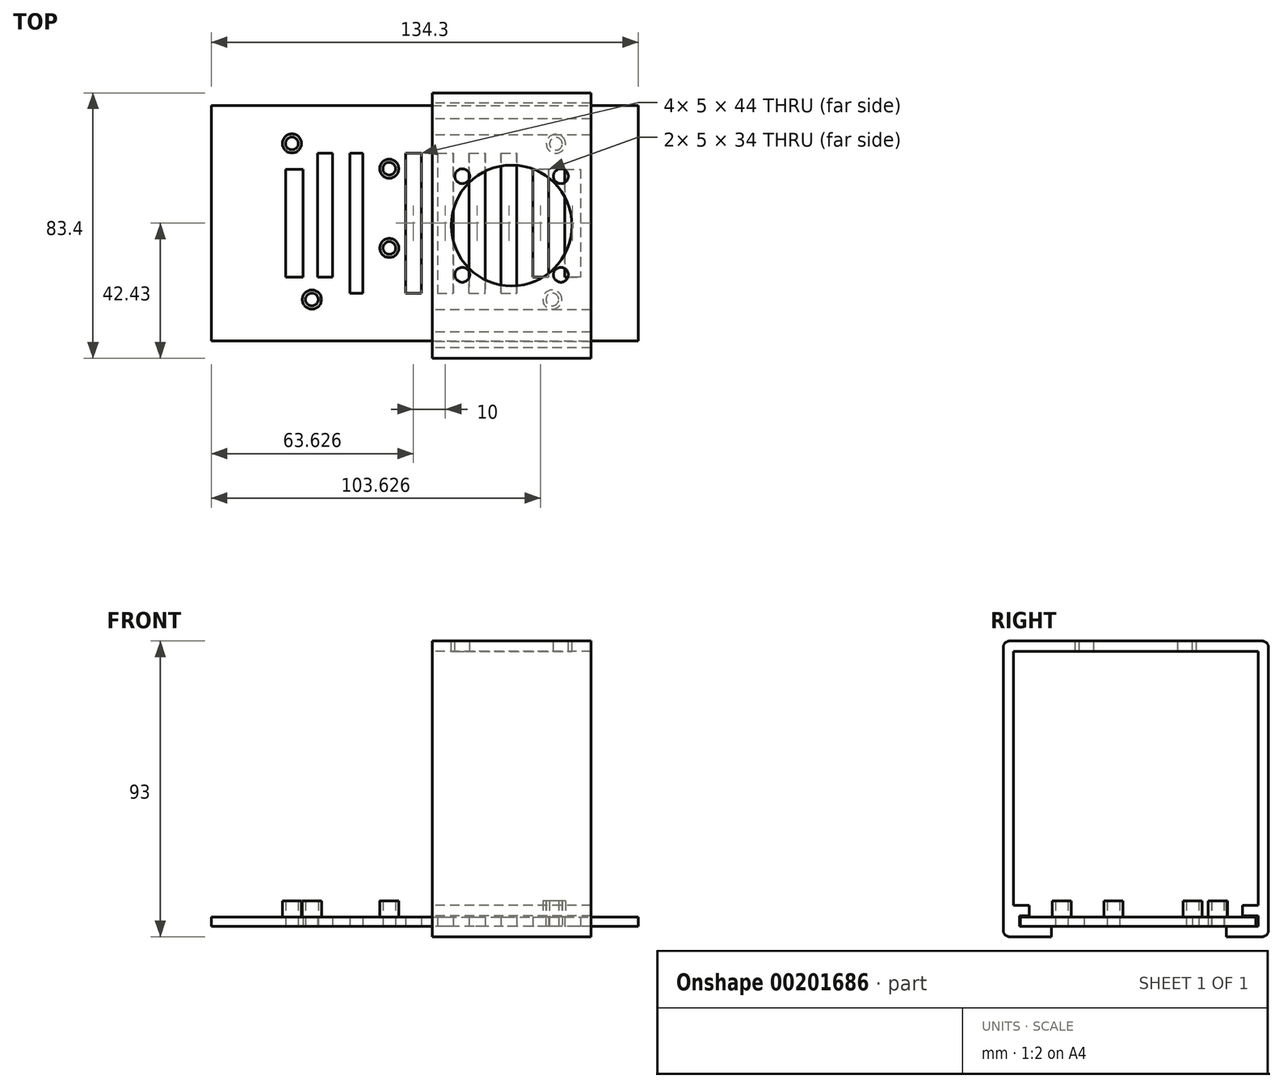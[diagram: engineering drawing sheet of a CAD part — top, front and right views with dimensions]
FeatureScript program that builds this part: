
annotation { "Feature Type Name" : "Feature", "Feature Type Description" : "" }
export const myFeature = defineFeature(function(context is Context, id is Id, definition is map)
    precondition{}
    {
        {
            var Q0;
            Q0=qCreatedBy(makeId("Top.planeOp"),FACE);
            var sketch = newSketch(context, id + "F0", { "sketchPlane" : qUnion([Q0])});
            skLineSegment(sketch, "E0.bottom", {"start": v(-46.5, 27) * mm, "end": v(48, 27) * mm});
            skLineSegment(sketch, "E0.top", {"start": v(-46.75, -27) * mm, "end": v(48, -27) * mm});
            skLineSegment(sketch, "E0.left", {"start": v(-49.5, 22.5) * mm, "end": v(-49.5, -14.5) * mm});
            skLineSegment(sketch, "E0.right", {"start": v(48, 27) * mm, "end": v(48, 23.31) * mm});
            skCircle(sketch, "E1", {"center": v(-44.1, 25.1) * mm, "radius": 2 * mm});
            skCircle(sketch, "E2", {"center": v(-37.82, -24) * mm, "radius": 2 * mm});
            skCircle(sketch, "E3", {"center": v(-13.47, -7.8) * mm, "radius": 2 * mm});
            skCircle(sketch, "E4", {"center": v(38.9, 24.99) * mm, "radius": 2 * mm});
            skCircle(sketch, "E5", {"center": v(37.78, -24) * mm, "radius": 2 * mm});
            skLineSegment(sketch, "E6.bottom", {"start": v(-49.5, -14.5) * mm, "end": v(-46.75, -14.5) * mm});
            skLineSegment(sketch, "E6.right", {"start": v(-46.75, -14.5) * mm, "end": v(-46.75, -27) * mm});
            skCircle(sketch, "E7", {"center": v(-13.52, 17.15) * mm, "radius": 2 * mm});
            skLineSegment(sketch, "E8.bottom", {"start": v(48, -17.5) * mm, "end": v(54.8, -17.5) * mm});
            skLineSegment(sketch, "E8.top", {"start": v(48, -5.37) * mm, "end": v(54.8, -5.37) * mm});
            skLineSegment(sketch, "E8.right", {"start": v(54.8, -17.5) * mm, "end": v(54.8, -5.37) * mm});
            skLineSegment(sketch, "E9.bottom", {"start": v(48, 23.31) * mm, "end": v(49.6, 23.31) * mm});
            skLineSegment(sketch, "E9.top", {"start": v(48, 14.31) * mm, "end": v(49.6, 14.31) * mm});
            skLineSegment(sketch, "E9.right", {"start": v(49.6, 23.31) * mm, "end": v(49.6, 14.31) * mm});
            skLineSegment(sketch, "E10.trimOffspring", {"start": v(48, 14.31) * mm, "end": v(48, -5.37) * mm});
            skLineSegment(sketch, "E11.trimOffspring", {"start": v(48, -17.5) * mm, "end": v(48, -27) * mm});
            skLineSegment(sketch, "E12", {"start": v(-49.5, 22.5) * mm, "end": v(-46.5, 27) * mm});
            skLineSegment(sketch, "E13.bottom", {"start": v(-69.5, -37) * mm, "end": v(64.8, -37) * mm});
            skLineSegment(sketch, "E13.left", {"start": v(-69.5, -37) * mm, "end": v(-69.5, 37) * mm});
            skLineSegment(sketch, "E13.right", {"start": v(64.8, -37) * mm, "end": v(64.8, 37) * mm});
            skLineSegment(sketch, "E14", {"start": v(-69.5, 37) * mm, "end": v(64.8, 37) * mm});
            skSolve(sketch);
        }
        {
            var Q0;
            Q0=makeQuery(id+"F0.imprint","IMPRINT",FACE,{"disambiguationData":[TD([[makeQuery(id+"F0.imprint","IMPRINT",EDGE,{"derivedFrom":sQuery(id+"F0.wireOp",EDGE,"E0.top")}),-1.0]])]});
            var Q1;
            Q1=makeQuery(id+"F0.imprint","IMPRINT",FACE,{"disambiguationData":[TD([[makeQuery(id+"F0.imprint","IMPRINT",EDGE,{"derivedFrom":sQuery(id+"F0.wireOp",EDGE,"E0.top")}),1.0]])]});
            var Q2;
            {var subQ4=sQuery(id+"F0.wireOp",EDGE,"YDJerWL3-jqRJ-SHca-BXGt-VWNdCpcU7x4v.top");Q2=makeQuery(id+"F0.imprint","IMPRINT",FACE,{"disambiguationData":[TD([[makeQuery(id+"F0.imprint","IMPRINT",EDGE,{"derivedFrom":subQ4}),-1.0]])]});}
            extrude(context, id + "F1", {"entities" : qUnion([Q0, Q1, Q2]), "depth" : 3 * mm});
        }
        {
            var Q0;
            Q0=makeQuery(id+"F0.imprint","IMPRINT",FACE,{"disambiguationData":[TD([[makeQuery(id+"F0.imprint","IMPRINT",EDGE,{"derivedFrom":sQuery(id+"F0.wireOp",EDGE,"SJM5vi3X-GDIr-rpcV-fpPG-NIFEtbxejTYG")}),1.0]])]});
            var Q1;
            Q1=makeQuery(id+"F0.imprint","IMPRINT",FACE,{"disambiguationData":[TD([[makeQuery(id+"F0.imprint","IMPRINT",EDGE,{"derivedFrom":sQuery(id+"F0.wireOp",EDGE,"0b19459e-4994-4584-9e19-4744f961bc32")}),1.0]])]});
            var Q2;
            Q2=makeQuery(id+"F0.imprint","IMPRINT",FACE,{"disambiguationData":[TD([[makeQuery(id+"F0.imprint","IMPRINT",EDGE,{"derivedFrom":sQuery(id+"F0.wireOp",EDGE,"b25e501f-24e3-4316-b24d-71f173e7bc01")}),1.0]])]});
            var Q3;
            Q3=makeQuery(id+"F0.imprint","IMPRINT",FACE,{"disambiguationData":[TD([[makeQuery(id+"F0.imprint","IMPRINT",EDGE,{"derivedFrom":sQuery(id+"F0.wireOp",EDGE,"ed0e2581-f028-4d6a-86a3-a8fe110090f4")}),1.0]])]});
            var Q4;
            Q4=makeQuery(id+"F0.imprint","IMPRINT",FACE,{"disambiguationData":[TD([[makeQuery(id+"F0.imprint","IMPRINT",EDGE,{"derivedFrom":sQuery(id+"F0.wireOp",EDGE,"E1")}),1.0]])]});
            var Q5;
            Q5=makeQuery(id+"F0.imprint","IMPRINT",FACE,{"disambiguationData":[TD([[makeQuery(id+"F0.imprint","IMPRINT",EDGE,{"derivedFrom":sQuery(id+"F0.wireOp",EDGE,"E7")}),1.0]])]});
            var Q6;
            Q6=makeQuery(id+"F0.imprint","IMPRINT",FACE,{"disambiguationData":[TD([[makeQuery(id+"F0.imprint","IMPRINT",EDGE,{"derivedFrom":sQuery(id+"F0.wireOp",EDGE,"E4")}),1.0]])]});
            var Q7;
            Q7=makeQuery(id+"F0.imprint","IMPRINT",FACE,{"disambiguationData":[TD([[makeQuery(id+"F0.imprint","IMPRINT",EDGE,{"derivedFrom":sQuery(id+"F0.wireOp",EDGE,"E3")}),1.0]])]});
            var Q8;
            Q8=makeQuery(id+"F0.imprint","IMPRINT",FACE,{"disambiguationData":[TD([[makeQuery(id+"F0.imprint","IMPRINT",EDGE,{"derivedFrom":sQuery(id+"F0.wireOp",EDGE,"E2")}),1.0]])]});
            var Q9;
            Q9=makeQuery(id+"F0.imprint","IMPRINT",FACE,{"disambiguationData":[TD([[makeQuery(id+"F0.imprint","IMPRINT",EDGE,{"derivedFrom":sQuery(id+"F0.wireOp",EDGE,"E5")}),1.0]])]});
            extrude(context, id + "F2", {"entities" : qUnion([Q0, Q1, Q2, Q3, Q4, Q5, Q6, Q7, Q8, Q9]), "operationType" : NewBodyOperationType.REMOVE, "depth" : 25 * mm});
        }
        {
            var Q0;
            Q0=makeQuery(id+"F1.opExtrude","CAP_FACE",FACE,{"disambiguationData":[OSD([sQuery(id+"F0.wireOp",EDGE,"E1"),sQuery(id+"F0.wireOp",EDGE,"E2"),sQuery(id+"F0.wireOp",EDGE,"E3"),sQuery(id+"F0.wireOp",EDGE,"E4"),sQuery(id+"F0.wireOp",EDGE,"E5"),sQuery(id+"F0.wireOp",EDGE,"E7"),sQuery(id+"F0.wireOp",EDGE,"E13.bottom"),sQuery(id+"F0.wireOp",EDGE,"E13.top"),sQuery(id+"F0.wireOp",EDGE,"E13.left"),sQuery(id+"F0.wireOp",EDGE,"E13.right"),sQuery(id+"F0.wireOp",EDGE,"SJM5vi3X-GDIr-rpcV-fpPG-NIFEtbxejTYG"),sQuery(id+"F0.wireOp",EDGE,"0b19459e-4994-4584-9e19-4744f961bc32"),sQuery(id+"F0.wireOp",EDGE,"b25e501f-24e3-4316-b24d-71f173e7bc01"),sQuery(id+"F0.wireOp",EDGE,"ed0e2581-f028-4d6a-86a3-a8fe110090f4")])],"isStart":false});
            var sketch = newSketch(context, id + "F3", { "sketchPlane" : qUnion([Q0])});
            skCircle(sketch, "E15", {"center": v(-44.1, 25.1) * mm, "radius": 3 * mm});
            skCircle(sketch, "E16", {"center": v(-44.1, 25.1) * mm, "radius": 2 * mm});
            skCircle(sketch, "E17", {"center": v(-13.52, 17.15) * mm, "radius": 2 * mm});
            skCircle(sketch, "E18", {"center": v(-13.52, 17.15) * mm, "radius": 3 * mm});
            skCircle(sketch, "E19", {"center": v(38.9, 24.99) * mm, "radius": 3 * mm});
            skCircle(sketch, "E20", {"center": v(38.9, 24.99) * mm, "radius": 2 * mm});
            skCircle(sketch, "E21", {"center": v(-13.47, -7.8) * mm, "radius": 2 * mm});
            skCircle(sketch, "E22", {"center": v(-13.47, -7.8) * mm, "radius": 3 * mm});
            skCircle(sketch, "E23", {"center": v(-37.82, -24) * mm, "radius": 2 * mm});
            skCircle(sketch, "E24", {"center": v(-37.82, -24) * mm, "radius": 3 * mm});
            skCircle(sketch, "E25", {"center": v(37.78, -24) * mm, "radius": 2 * mm});
            skCircle(sketch, "E26", {"center": v(37.78, -24) * mm, "radius": 3 * mm});
            skSolve(sketch);
        }
        {
            var Q0;
            Q0=makeQuery(id+"F3.imprint","IMPRINT",FACE,{"disambiguationData":[TD([[makeQuery(id+"F3.imprint","IMPRINT",EDGE,{"derivedFrom":sQuery(id+"F3.wireOp",EDGE,"Aj7JneEY-PVIe-ZHZf-ZIJg-59aWa9WPDq15")}),1.0]])]});
            var Q1;
            Q1=makeQuery(id+"F3.imprint","IMPRINT",FACE,{"disambiguationData":[TD([[makeQuery(id+"F3.imprint","IMPRINT",EDGE,{"derivedFrom":sQuery(id+"F3.wireOp",EDGE,"Z7iTzPcF-sDzZ-Ksxt-ygBO-0pxRtejIhL9z")}),1.0]])]});
            var Q2;
            Q2=makeQuery(id+"F3.imprint","IMPRINT",FACE,{"disambiguationData":[TD([[makeQuery(id+"F3.imprint","IMPRINT",EDGE,{"derivedFrom":sQuery(id+"F3.wireOp",EDGE,"83ZUaEs0-tj28-sCEl-sk6l-ODubapMiD2mB")}),-1.0]])]});
            var Q3;
            Q3=makeQuery(id+"F3.imprint","IMPRINT",FACE,{"disambiguationData":[TD([[makeQuery(id+"F3.imprint","IMPRINT",EDGE,{"derivedFrom":sQuery(id+"F3.wireOp",EDGE,"rJwicVRi-7QL9-MqIy-NEF6-RD9lB6ido8TI")}),-1.0]])]});
            var Q4;
            Q4=makeQuery(id+"F3.imprint","IMPRINT",FACE,{"disambiguationData":[TD([[makeQuery(id+"F3.imprint","IMPRINT",EDGE,{"derivedFrom":sQuery(id+"F3.wireOp",EDGE,"E15")}),1.0]])]});
            var Q5;
            Q5=makeQuery(id+"F3.imprint","IMPRINT",FACE,{"disambiguationData":[TD([[makeQuery(id+"F3.imprint","IMPRINT",EDGE,{"derivedFrom":sQuery(id+"F3.wireOp",EDGE,"E17")}),-1.0]])]});
            var Q6;
            Q6=makeQuery(id+"F3.imprint","IMPRINT",FACE,{"disambiguationData":[TD([[makeQuery(id+"F3.imprint","IMPRINT",EDGE,{"derivedFrom":sQuery(id+"F3.wireOp",EDGE,"E19")}),1.0]])]});
            var Q7;
            Q7=makeQuery(id+"F3.imprint","IMPRINT",FACE,{"disambiguationData":[TD([[makeQuery(id+"F3.imprint","IMPRINT",EDGE,{"derivedFrom":sQuery(id+"F3.wireOp",EDGE,"E21")}),-1.0]])]});
            var Q8;
            Q8=makeQuery(id+"F3.imprint","IMPRINT",FACE,{"disambiguationData":[TD([[makeQuery(id+"F3.imprint","IMPRINT",EDGE,{"derivedFrom":sQuery(id+"F3.wireOp",EDGE,"E23")}),-1.0]])]});
            var Q9;
            Q9=makeQuery(id+"F3.imprint","IMPRINT",FACE,{"disambiguationData":[TD([[makeQuery(id+"F3.imprint","IMPRINT",EDGE,{"derivedFrom":sQuery(id+"F3.wireOp",EDGE,"E25")}),-1.0]])]});
            extrude(context, id + "F4", {"entities" : qUnion([Q0, Q1, Q2, Q3, Q4, Q5, Q6, Q7, Q8, Q9]), "operationType" : NewBodyOperationType.ADD, "depth" : 5 * mm});
        }
        {
            var Q0;
            Q0=makeQuery(id+"F1.opExtrude","CAP_FACE",FACE,{"disambiguationData":[OSD([sQuery(id+"F0.wireOp",EDGE,"E1"),sQuery(id+"F0.wireOp",EDGE,"E2"),sQuery(id+"F0.wireOp",EDGE,"E3"),sQuery(id+"F0.wireOp",EDGE,"E4"),sQuery(id+"F0.wireOp",EDGE,"E5"),sQuery(id+"F0.wireOp",EDGE,"E7"),sQuery(id+"F0.wireOp",EDGE,"E13.bottom"),sQuery(id+"F0.wireOp",EDGE,"E13.top"),sQuery(id+"F0.wireOp",EDGE,"E13.left"),sQuery(id+"F0.wireOp",EDGE,"E13.right"),sQuery(id+"F0.wireOp",EDGE,"SJM5vi3X-GDIr-rpcV-fpPG-NIFEtbxejTYG"),sQuery(id+"F0.wireOp",EDGE,"0b19459e-4994-4584-9e19-4744f961bc32"),sQuery(id+"F0.wireOp",EDGE,"b25e501f-24e3-4316-b24d-71f173e7bc01"),sQuery(id+"F0.wireOp",EDGE,"ed0e2581-f028-4d6a-86a3-a8fe110090f4")])],"isStart":false});
            var sketch = newSketch(context, id + "F5", { "sketchPlane" : qUnion([Q0])});
            skSolve(sketch);
        }
        {
            var Q0;
            Q0=qCreatedBy(makeId("Right.planeOp"),FACE);
            var sketch = newSketch(context, id + "F6", { "sketchPlane" : qUnion([Q0])});
            skSolve(sketch);
        }
        {
            var Q0;
            Q0=makeQuery(id+"F0.imprint","IMPRINT",FACE,{"disambiguationData":[TD([[makeQuery(id+"F0.imprint","IMPRINT",EDGE,{"derivedFrom":sQuery(id+"F0.wireOp",EDGE,"E0.bottom")}),1.0]])]});
            var sketch = newSketch(context, id + "F7", { "sketchPlane" : qUnion([Q0])});
            skLineSegment(sketch, "E27.bottom", {"start": v(46.63, -17) * mm, "end": v(41.63, -17) * mm});
            skLineSegment(sketch, "E27.top", {"start": v(46.63, 17) * mm, "end": v(41.63, 17) * mm});
            skLineSegment(sketch, "E27.left", {"start": v(46.63, -17) * mm, "end": v(46.63, 17) * mm});
            skLineSegment(sketch, "E27.right", {"start": v(41.63, -17) * mm, "end": v(41.63, 17) * mm});
            skLineSegment(sketch, "E28.bottom", {"start": v(26.63, -22) * mm, "end": v(21.63, -22) * mm});
            skLineSegment(sketch, "E28.top", {"start": v(26.63, 22) * mm, "end": v(21.63, 22) * mm});
            skLineSegment(sketch, "E28.left", {"start": v(26.63, -22) * mm, "end": v(26.63, 22) * mm});
            skLineSegment(sketch, "E28.right", {"start": v(21.63, -22) * mm, "end": v(21.63, 22) * mm});
            skLineSegment(sketch, "E29.bottom", {"start": v(16.63, -22) * mm, "end": v(11.63, -22) * mm});
            skLineSegment(sketch, "E29.top", {"start": v(16.63, 22) * mm, "end": v(11.63, 22) * mm});
            skLineSegment(sketch, "E29.left", {"start": v(16.63, -22) * mm, "end": v(16.63, 22) * mm});
            skLineSegment(sketch, "E29.right", {"start": v(11.63, -22) * mm, "end": v(11.63, 22) * mm});
            skLineSegment(sketch, "E30.bottom", {"start": v(6.63, -22) * mm, "end": v(1.63, -22) * mm});
            skLineSegment(sketch, "E30.top", {"start": v(6.63, 22) * mm, "end": v(1.63, 22) * mm});
            skLineSegment(sketch, "E30.left", {"start": v(6.63, -22) * mm, "end": v(6.63, 22) * mm});
            skLineSegment(sketch, "E30.right", {"start": v(1.63, -22) * mm, "end": v(1.63, 22) * mm});
            skLineSegment(sketch, "E31.bottom", {"start": v(-3.37, -22) * mm, "end": v(-8.37, -22) * mm});
            skLineSegment(sketch, "E31.top", {"start": v(-3.37, 22) * mm, "end": v(-8.37, 22) * mm});
            skLineSegment(sketch, "E31.left", {"start": v(-8.37, -22) * mm, "end": v(-8.37, 22) * mm});
            skLineSegment(sketch, "E31.right", {"start": v(-3.37, -22) * mm, "end": v(-3.37, 22) * mm});
            skLineSegment(sketch, "E32.bottom", {"start": v(-21.75, -22) * mm, "end": v(-25.92, -22) * mm});
            skLineSegment(sketch, "E32.top", {"start": v(-21.75, 22) * mm, "end": v(-25.92, 22) * mm});
            skLineSegment(sketch, "E32.left", {"start": v(-21.75, -22) * mm, "end": v(-21.75, 22) * mm});
            skLineSegment(sketch, "E32.right", {"start": v(-25.92, -22) * mm, "end": v(-25.92, 22) * mm});
            skLineSegment(sketch, "E33.bottom", {"start": v(-31.32, -17) * mm, "end": v(-35.99, -17) * mm});
            skLineSegment(sketch, "E33.top", {"start": v(-31.32, 22) * mm, "end": v(-35.99, 22) * mm});
            skLineSegment(sketch, "E33.left", {"start": v(-31.32, -17) * mm, "end": v(-31.32, 22) * mm});
            skLineSegment(sketch, "E33.right", {"start": v(-35.99, -17) * mm, "end": v(-35.99, 22) * mm});
            skLineSegment(sketch, "E34.bottom", {"start": v(-40.65, -17) * mm, "end": v(-46.05, -17) * mm});
            skLineSegment(sketch, "E34.top", {"start": v(-40.65, 17) * mm, "end": v(-46.05, 17) * mm});
            skLineSegment(sketch, "E34.left", {"start": v(-40.65, -17) * mm, "end": v(-40.65, 17) * mm});
            skLineSegment(sketch, "E34.right", {"start": v(-46.05, -17) * mm, "end": v(-46.05, 17) * mm});
            skPoint(sketch, "E35.right.end.orphan", {"position": v(31.63, 17) * mm});
            skLineSegment(sketch, "E36.bottom", {"start": v(36.63, -17) * mm, "end": v(31.63, -17) * mm});
            skLineSegment(sketch, "E36.top", {"start": v(36.63, 17) * mm, "end": v(31.63, 17) * mm});
            skLineSegment(sketch, "E36.left", {"start": v(36.63, -17) * mm, "end": v(36.63, 17) * mm});
            skLineSegment(sketch, "E36.right", {"start": v(31.63, -17) * mm, "end": v(31.63, 17) * mm});
            skSolve(sketch);
        }
        {
            var Q0;
            Q0=qSketchRegion(id+"F7",true);
            extrude(context, id + "F8", {"entities" : qUnion([Q0]), "operationType" : NewBodyOperationType.REMOVE, "depth" : 25 * mm});
        }
        {
            var Q0;
            Q0=qCreatedBy(makeId("Right.planeOp"),FACE);
            var sketch = newSketch(context, id + "F9", { "sketchPlane" : qUnion([Q0])});
            skLineSegment(sketch, "E37", {"start": v(-37.25, 0) * mm, "end": v(-27.25, 0) * mm});
            skLineSegment(sketch, "E38", {"start": v(-27.25, 0) * mm, "end": v(-27.25, -3.2) * mm});
            skLineSegment(sketch, "E39", {"start": v(-27.25, -3.2) * mm, "end": v(-42.43, -3.2) * mm});
            skLineSegment(sketch, "E40", {"start": v(-42.43, -3.2) * mm, "end": v(-42.43, 89.8) * mm});
            skLineSegment(sketch, "E41", {"start": v(-42.43, 89.8) * mm, "end": v(40.97, 89.8) * mm});
            skLineSegment(sketch, "E42", {"start": v(40.97, 89.8) * mm, "end": v(40.97, -3.2) * mm});
            skLineSegment(sketch, "E43", {"start": v(40.97, -3.2) * mm, "end": v(27.77, -3.2) * mm});
            skLineSegment(sketch, "E44", {"start": v(27.77, -3.2) * mm, "end": v(27.77, 0) * mm});
            skLineSegment(sketch, "E45", {"start": v(27.77, 0) * mm, "end": v(37.77, 0) * mm});
            skLineSegment(sketch, "E46", {"start": v(37.77, 0) * mm, "end": v(37.77, 3.4) * mm});
            skLineSegment(sketch, "E47", {"start": v(37.77, 6.6) * mm, "end": v(32.77, 6.6) * mm});
            skLineSegment(sketch, "E48", {"start": v(32.77, 3.4) * mm, "end": v(32.77, 6.6) * mm});
            skLineSegment(sketch, "E49", {"start": v(32.77, 3.4) * mm, "end": v(37.77, 3.4) * mm});
            skLineSegment(sketch, "E50", {"start": v(37.77, 6.6) * mm, "end": v(37.77, 86.6) * mm});
            skLineSegment(sketch, "E51", {"start": v(37.77, 86.6) * mm, "end": v(-39.23, 86.6) * mm});
            skLineSegment(sketch, "E52", {"start": v(-39.23, 86.6) * mm, "end": v(-39.23, 6.6) * mm});
            skLineSegment(sketch, "E53", {"start": v(-39.23, 6.6) * mm, "end": v(-34.23, 6.6) * mm});
            skLineSegment(sketch, "E54", {"start": v(-34.23, 6.6) * mm, "end": v(-34.23, 3.4) * mm});
            skLineSegment(sketch, "E55", {"start": v(-34.23, 3.4) * mm, "end": v(-37.25, 3.4) * mm});
            skLineSegment(sketch, "E56", {"start": v(-37.25, 3.4) * mm, "end": v(-37.25, 0) * mm});
            skSolve(sketch);
        }
        {
            var Q0;
            Q0=makeQuery(id+"F9.imprint","IMPRINT",FACE,{"disambiguationData":[TD([[makeQuery(id+"F9.imprint","IMPRINT",EDGE,{"derivedFrom":sQuery(id+"F9.wireOp",EDGE,"E37")}),-1.0]])]});
            extrude(context, id + "F10", {"entities" : qUnion([Q0]), "depth" : 50 * mm});
        }
        {
            var Q0;
            Q0=makeQuery(id+"F10.opExtrude","SWEPT_FACE",FACE,{"disambiguationData":[OSD([sQuery(id+"F9.wireOp",EDGE,"E41")])]});
            var sketch = newSketch(context, id + "F11", { "sketchPlane" : qUnion([Q0])});
            skLineSegment(sketch, "E57.bottom", {"start": v(4.98, -20.73) * mm, "end": v(44.98, -20.73) * mm});
            skLineSegment(sketch, "E57.top", {"start": v(4.98, 19.27) * mm, "end": v(44.98, 19.27) * mm});
            skLineSegment(sketch, "E57.left", {"start": v(4.98, -20.73) * mm, "end": v(4.98, 19.27) * mm});
            skLineSegment(sketch, "E57.right", {"start": v(44.98, -20.73) * mm, "end": v(44.98, 19.27) * mm});
            skCircle(sketch, "E58", {"center": v(9.48, -16.23) * mm, "radius": 2.34 * mm});
            skCircle(sketch, "E59", {"center": v(40.48, -16.23) * mm, "radius": 2.34 * mm});
            skCircle(sketch, "E60", {"center": v(9.48, 14.77) * mm, "radius": 2.34 * mm});
            skCircle(sketch, "E61", {"center": v(40.48, 14.77) * mm, "radius": 2.34 * mm});
            skCircle(sketch, "E62", {"center": v(24.98, -0.73) * mm, "radius": 19 * mm});
            skPoint(sketch, "E62.centerSnap0", {"position": v(4.98, -0.73) * mm});
            skPoint(sketch, "E62.centerSnap1", {"position": v(24.98, -20.73) * mm});
            skSolve(sketch);
        }
        {
            var Q0;
            Q0=makeQuery(id+"F11.imprint","IMPRINT",FACE,{"disambiguationData":[TD([[makeQuery(id+"F11.imprint","IMPRINT",EDGE,{"derivedFrom":sQuery(id+"F11.wireOp",EDGE,"E58")}),1.0]])]});
            var Q1;
            Q1=makeQuery(id+"F11.imprint","IMPRINT",FACE,{"disambiguationData":[TD([[makeQuery(id+"F11.imprint","IMPRINT",EDGE,{"derivedFrom":sQuery(id+"F11.wireOp",EDGE,"E62")}),1.0]])]});
            var Q2;
            Q2=makeQuery(id+"F11.imprint","IMPRINT",FACE,{"disambiguationData":[TD([[makeQuery(id+"F11.imprint","IMPRINT",EDGE,{"derivedFrom":sQuery(id+"F11.wireOp",EDGE,"E60")}),1.0]])]});
            var Q3;
            Q3=makeQuery(id+"F11.imprint","IMPRINT",FACE,{"disambiguationData":[TD([[makeQuery(id+"F11.imprint","IMPRINT",EDGE,{"derivedFrom":sQuery(id+"F11.wireOp",EDGE,"E61")}),1.0]])]});
            var Q4;
            Q4=makeQuery(id+"F11.imprint","IMPRINT",FACE,{"disambiguationData":[TD([[makeQuery(id+"F11.imprint","IMPRINT",EDGE,{"derivedFrom":sQuery(id+"F11.wireOp",EDGE,"E59")}),1.0]])]});
            extrude(context, id + "F12", {"entities" : qUnion([Q0, Q1, Q2, Q3, Q4]), "operationType" : NewBodyOperationType.REMOVE, "oppositeDirection" : true, "depth" : 25 * mm});
        }
        {
            var Q0;
            Q0=makeQuery(id+"F10.opExtrude","SWEPT_EDGE",EDGE,{"disambiguationData":[OSD([sQuery(id+"F9.wireOp",EDGE,"E42"),sQuery(id+"F9.wireOp",EDGE,"E43")])]});
            var Q1;
            Q1=makeQuery(id+"F10.opExtrude","SWEPT_EDGE",EDGE,{"disambiguationData":[OSD([sQuery(id+"F9.wireOp",EDGE,"E39"),sQuery(id+"F9.wireOp",EDGE,"E40")])]});
            var Q2;
            Q2=makeQuery(id+"F10.opExtrude","SWEPT_EDGE",EDGE,{"disambiguationData":[OSD([sQuery(id+"F9.wireOp",EDGE,"E41"),sQuery(id+"F9.wireOp",EDGE,"E42")])]});
            var Q3;
            Q3=makeQuery(id+"F10.opExtrude","SWEPT_EDGE",EDGE,{"disambiguationData":[OSD([sQuery(id+"F9.wireOp",EDGE,"E40"),sQuery(id+"F9.wireOp",EDGE,"E41")])]});
            fillet(context, id + "F13", {"entities" : qUnion([Q0, Q1, Q2, Q3]), "radius" : 2 * mm, "tangentPropagation" : true, "allowEdgeOverflow" : false});
        }
    });
